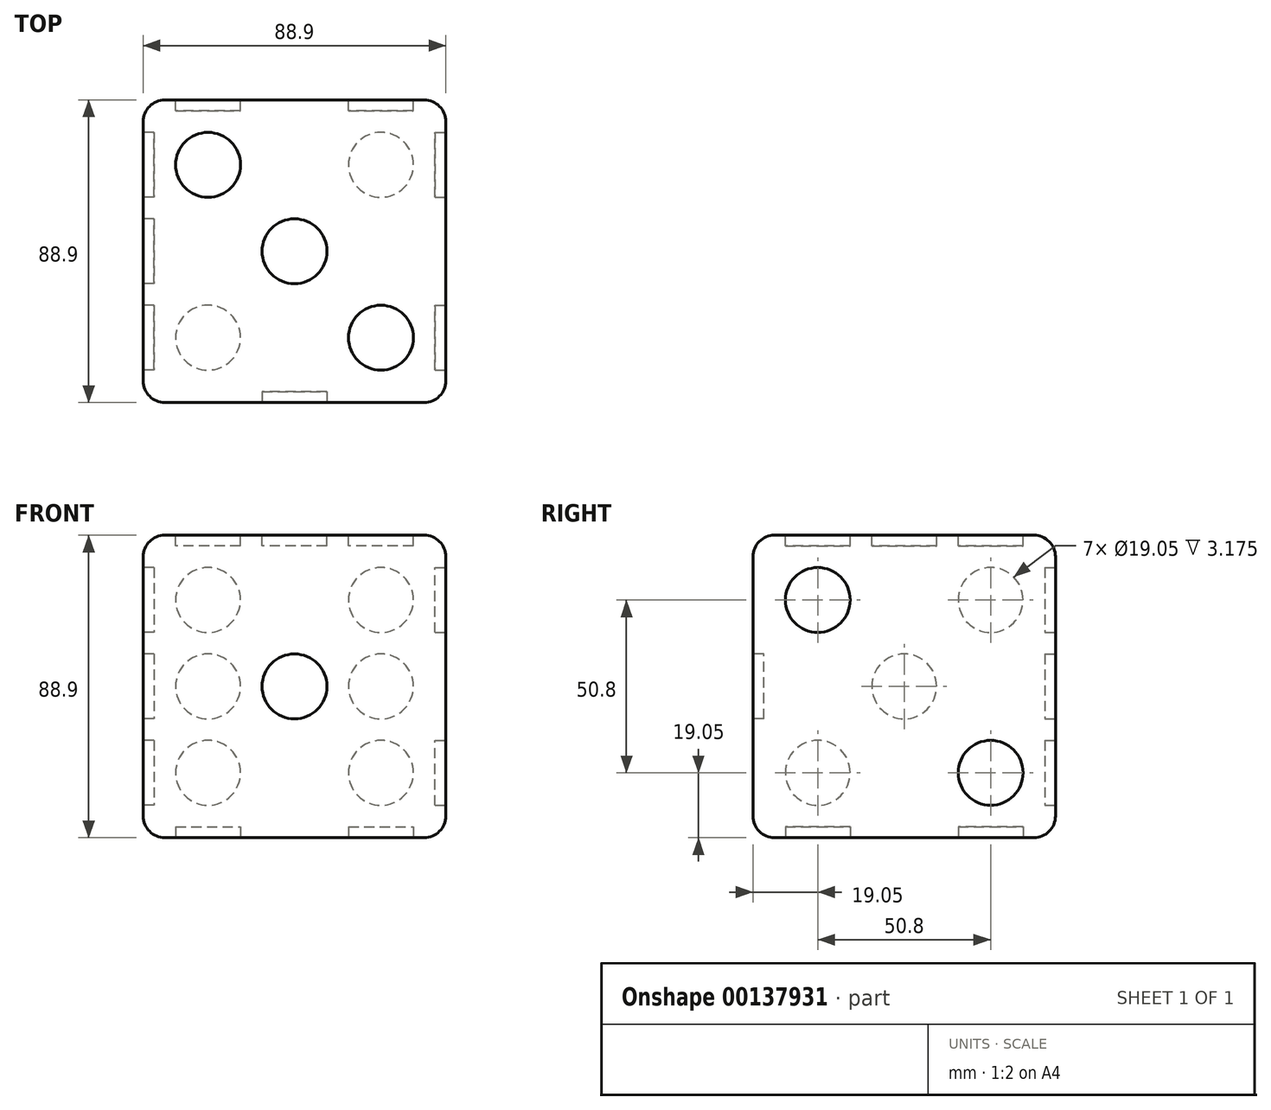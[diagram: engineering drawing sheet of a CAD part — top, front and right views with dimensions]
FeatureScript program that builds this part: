
annotation { "Feature Type Name" : "Feature", "Feature Type Description" : "" }
export const myFeature = defineFeature(function(context is Context, id is Id, definition is map)
    precondition{}
    {
        {
            var Q0;
            Q0=qCreatedBy(makeId("Top.planeOp"),FACE);
            var sketch = newSketch(context, id + "F0", { "sketchPlane" : qUnion([Q0])});
            skLineSegment(sketch, "E0.bottom", {"start": v(44.45, -44.45) * mm, "end": v(-44.45, -44.45) * mm});
            skLineSegment(sketch, "E0.top", {"start": v(44.45, 44.45) * mm, "end": v(-44.45, 44.45) * mm});
            skLineSegment(sketch, "E0.left", {"start": v(44.45, -44.45) * mm, "end": v(44.45, 44.45) * mm});
            skLineSegment(sketch, "E0.right", {"start": v(-44.45, -44.45) * mm, "end": v(-44.45, 44.45) * mm});
            skPoint(sketch, "E0.middle", {"position": v(0, 0) * mm});
            skSolve(sketch);
        }
        {
            var Q0;
            Q0 = qSketchRegion(id + "F0", true);
            extrude(context, id + "F1", {"entities" : qUnion([Q0]), "depth" : 88.9 * mm, "symmetric" : true});
        }
        {
            var Q0;
            Q0=makeQuery(id+"F1.opExtrude","CAP_FACE",FACE,{"disambiguationData":[OSD([sQuery(id+"F0.wireOp",EDGE,"E0.bottom"),sQuery(id+"F0.wireOp",EDGE,"E0.top"),sQuery(id+"F0.wireOp",EDGE,"E0.left"),sQuery(id+"F0.wireOp",EDGE,"E0.right")])],"isStart":false});
            var Q1;
            Q1=makeQuery(id+"F1.opExtrude","SWEPT_FACE",FACE,{"disambiguationData":[OSD([sQuery(id+"F0.wireOp",EDGE,"E0.bottom")])]});
            var Q2;
            Q2=makeQuery(id+"F1.opExtrude","SWEPT_FACE",FACE,{"disambiguationData":[OSD([sQuery(id+"F0.wireOp",EDGE,"E0.top")])]});
            var Q3;
            Q3=makeQuery(id+"F1.opExtrude","CAP_FACE",FACE,{"disambiguationData":[OSD([sQuery(id+"F0.wireOp",EDGE,"E0.bottom"),sQuery(id+"F0.wireOp",EDGE,"E0.top"),sQuery(id+"F0.wireOp",EDGE,"E0.left"),sQuery(id+"F0.wireOp",EDGE,"E0.right")])],"isStart":true});
            fillet(context, id + "F2", {"entities" : qUnion([Q0, Q1, Q2, Q3]), "radius" : 6.35 * mm, "tangentPropagation" : true, "allowEdgeOverflow" : false});
        }
        {
            var Q0;
            Q0=makeQuery(id+"F1.opExtrude","SWEPT_FACE",FACE,{"disambiguationData":[OSD([sQuery(id+"F0.wireOp",EDGE,"E0.bottom")])]});
            var sketch = newSketch(context, id + "F3", { "sketchPlane" : qUnion([Q0])});
            skLineSegment(sketch, "E1.bottom", {"start": v(34.92, -34.92) * mm, "end": v(-34.92, -34.92) * mm, "construction": true});
            skLineSegment(sketch, "E1.top", {"start": v(34.92, 34.93) * mm, "end": v(-34.92, 34.93) * mm, "construction": true});
            skLineSegment(sketch, "E1.left", {"start": v(34.92, -34.93) * mm, "end": v(34.92, 34.93) * mm, "construction": true});
            skLineSegment(sketch, "E1.right", {"start": v(-34.92, -34.93) * mm, "end": v(-34.92, 34.93) * mm, "construction": true});
            skPoint(sketch, "E1.middle", {"position": v(0, 0) * mm});
            skLineSegment(sketch, "E2", {"start": v(0, 34.93) * mm, "end": v(0, -34.92) * mm, "construction": true});
            skLineSegment(sketch, "E3", {"start": v(34.92, 0) * mm, "end": v(-34.92, 0) * mm, "construction": true});
            skLineSegment(sketch, "E4", {"start": v(-25.4, 34.93) * mm, "end": v(-25.4, -34.92) * mm, "construction": true});
            skLineSegment(sketch, "E5", {"start": v(-34.92, -25.4) * mm, "end": v(34.92, -25.4) * mm, "construction": true});
            skLineSegment(sketch, "E6", {"start": v(25.4, 34.93) * mm, "end": v(25.4, -34.93) * mm, "construction": true});
            skLineSegment(sketch, "E7", {"start": v(-34.92, 25.4) * mm, "end": v(34.92, 25.4) * mm, "construction": true});
            skCircle(sketch, "E8", {"center": v(-25.4, 25.4) * mm, "radius": 9.52 * mm, "construction": true});
            skCircle(sketch, "E9", {"center": v(25.4, 25.4) * mm, "radius": 9.52 * mm, "construction": true});
            skCircle(sketch, "E10", {"center": v(-25.4, -25.4) * mm, "radius": 9.52 * mm, "construction": true});
            skCircle(sketch, "E11", {"center": v(25.4, -25.4) * mm, "radius": 9.52 * mm, "construction": true});
            skCircle(sketch, "E12", {"center": v(-25.4, 0) * mm, "radius": 9.52 * mm, "construction": true});
            skCircle(sketch, "E13", {"center": v(25.4, 0) * mm, "radius": 9.52 * mm, "construction": true});
            skCircle(sketch, "E14", {"center": v(0, 0) * mm, "radius": 9.52 * mm});
            skCircle(sketch, "E15", {"center": v(0, -25.4) * mm, "radius": 9.52 * mm, "construction": true});
            skCircle(sketch, "E16", {"center": v(0, 25.4) * mm, "radius": 9.52 * mm, "construction": true});
            skSolve(sketch);
        }
        {
            var Q0;
            Q0=makeQuery(id+"F1.opExtrude","CAP_FACE",FACE,{"disambiguationData":[OSD([sQuery(id+"F0.wireOp",EDGE,"E0.bottom"),sQuery(id+"F0.wireOp",EDGE,"E0.top"),sQuery(id+"F0.wireOp",EDGE,"E0.left"),sQuery(id+"F0.wireOp",EDGE,"E0.right")])],"isStart":true});
            var sketch = newSketch(context, id + "F4", { "sketchPlane" : qUnion([Q0])});
            skLineSegment(sketch, "E17.bottom", {"start": v(34.93, -34.93) * mm, "end": v(-34.93, -34.93) * mm, "construction": true});
            skLineSegment(sketch, "E17.top", {"start": v(34.92, 34.93) * mm, "end": v(-34.93, 34.93) * mm, "construction": true});
            skLineSegment(sketch, "E17.left", {"start": v(34.92, -34.93) * mm, "end": v(34.92, 34.93) * mm, "construction": true});
            skLineSegment(sketch, "E17.right", {"start": v(-34.93, -34.93) * mm, "end": v(-34.93, 34.93) * mm, "construction": true});
            skPoint(sketch, "E17.middle", {"position": v(0, 0) * mm});
            skLineSegment(sketch, "E18", {"start": v(0, 34.93) * mm, "end": v(0, -34.93) * mm, "construction": true});
            skLineSegment(sketch, "E19", {"start": v(34.93, 0) * mm, "end": v(-34.93, 0) * mm, "construction": true});
            skLineSegment(sketch, "E20", {"start": v(-25.4, 34.93) * mm, "end": v(-25.4, -34.93) * mm, "construction": true});
            skLineSegment(sketch, "E21", {"start": v(-34.92, -25.4) * mm, "end": v(34.92, -25.4) * mm, "construction": true});
            skLineSegment(sketch, "E22", {"start": v(25.4, 34.93) * mm, "end": v(25.4, -34.93) * mm, "construction": true});
            skLineSegment(sketch, "E23", {"start": v(-34.92, 25.4) * mm, "end": v(34.92, 25.4) * mm, "construction": true});
            skCircle(sketch, "E24", {"center": v(-25.4, 25.4) * mm, "radius": 9.52 * mm});
            skCircle(sketch, "E25", {"center": v(25.4, 25.4) * mm, "radius": 9.52 * mm});
            skCircle(sketch, "E26", {"center": v(-25.4, -25.4) * mm, "radius": 9.52 * mm});
            skCircle(sketch, "E27", {"center": v(25.4, -25.4) * mm, "radius": 9.52 * mm});
            skCircle(sketch, "E28", {"center": v(-25.4, 0) * mm, "radius": 9.52 * mm, "construction": true});
            skCircle(sketch, "E29", {"center": v(25.4, 0) * mm, "radius": 9.53 * mm, "construction": true});
            skCircle(sketch, "E30", {"center": v(0, 0) * mm, "radius": 9.52 * mm, "construction": true});
            skCircle(sketch, "E31", {"center": v(0, -25.4) * mm, "radius": 9.52 * mm, "construction": true});
            skCircle(sketch, "E32", {"center": v(0, 25.4) * mm, "radius": 9.52 * mm, "construction": true});
            skSolve(sketch);
        }
        {
            var Q0;
            Q0=makeQuery(id+"F1.opExtrude","SWEPT_FACE",FACE,{"disambiguationData":[OSD([sQuery(id+"F0.wireOp",EDGE,"E0.left")])]});
            var sketch = newSketch(context, id + "F5", { "sketchPlane" : qUnion([Q0])});
            skLineSegment(sketch, "E33.bottom", {"start": v(34.92, -34.93) * mm, "end": v(-34.92, -34.93) * mm, "construction": true});
            skLineSegment(sketch, "E33.top", {"start": v(34.92, 34.93) * mm, "end": v(-34.93, 34.93) * mm, "construction": true});
            skLineSegment(sketch, "E33.left", {"start": v(34.92, -34.93) * mm, "end": v(34.92, 34.93) * mm, "construction": true});
            skLineSegment(sketch, "E33.right", {"start": v(-34.92, -34.93) * mm, "end": v(-34.92, 34.92) * mm, "construction": true});
            skPoint(sketch, "E33.middle", {"position": v(0, 0) * mm});
            skLineSegment(sketch, "E34", {"start": v(0, 34.93) * mm, "end": v(0, -34.93) * mm, "construction": true});
            skLineSegment(sketch, "E35", {"start": v(34.92, 0) * mm, "end": v(-34.92, 0) * mm, "construction": true});
            skLineSegment(sketch, "E36", {"start": v(-25.4, 34.93) * mm, "end": v(-25.4, -34.93) * mm, "construction": true});
            skLineSegment(sketch, "E37", {"start": v(-34.92, -25.4) * mm, "end": v(34.92, -25.4) * mm, "construction": true});
            skLineSegment(sketch, "E38", {"start": v(25.4, 34.93) * mm, "end": v(25.4, -34.93) * mm, "construction": true});
            skLineSegment(sketch, "E39", {"start": v(-34.92, 25.4) * mm, "end": v(34.92, 25.4) * mm, "construction": true});
            skCircle(sketch, "E40", {"center": v(-25.4, 25.4) * mm, "radius": 9.53 * mm});
            skCircle(sketch, "E41", {"center": v(25.4, 25.4) * mm, "radius": 9.53 * mm, "construction": true});
            skCircle(sketch, "E42", {"center": v(-25.4, -25.4) * mm, "radius": 9.53 * mm, "construction": true});
            skCircle(sketch, "E43", {"center": v(25.4, -25.4) * mm, "radius": 9.53 * mm});
            skCircle(sketch, "E44", {"center": v(-25.4, 0) * mm, "radius": 9.53 * mm, "construction": true});
            skCircle(sketch, "E45", {"center": v(25.4, 0) * mm, "radius": 9.52 * mm, "construction": true});
            skCircle(sketch, "E46", {"center": v(0, 0) * mm, "radius": 9.53 * mm, "construction": true});
            skCircle(sketch, "E47", {"center": v(0, -25.4) * mm, "radius": 9.53 * mm, "construction": true});
            skCircle(sketch, "E48", {"center": v(0, 25.4) * mm, "radius": 9.53 * mm, "construction": true});
            skLineSegment(sketch, "E49.0.0", {"start": v(44.45, 38.1) * mm, "end": v(44.45, -38.1) * mm, "construction": true});
            skLineSegment(sketch, "E49.0.2", {"start": v(44.45, -38.1) * mm, "end": v(44.45, 38.1) * mm, "construction": true});
            skLineSegment(sketch, "E50.0.1", {"start": v(-38.1, -44.45) * mm, "end": v(38.1, -44.45) * mm, "construction": true});
            skLineSegment(sketch, "E50.0.3", {"start": v(38.1, -44.45) * mm, "end": v(-38.1, -44.45) * mm, "construction": true});
            skSolve(sketch);
        }
        {
            var Q0;
            Q0=makeQuery(id+"F1.opExtrude","CAP_FACE",FACE,{"disambiguationData":[OSD([sQuery(id+"F0.wireOp",EDGE,"E0.bottom"),sQuery(id+"F0.wireOp",EDGE,"E0.top"),sQuery(id+"F0.wireOp",EDGE,"E0.left"),sQuery(id+"F0.wireOp",EDGE,"E0.right")])],"isStart":false});
            var sketch = newSketch(context, id + "F6", { "sketchPlane" : qUnion([Q0])});
            skLineSegment(sketch, "E51.bottom", {"start": v(34.93, -34.92) * mm, "end": v(-34.92, -34.92) * mm, "construction": true});
            skLineSegment(sketch, "E51.top", {"start": v(34.92, 34.92) * mm, "end": v(-34.92, 34.92) * mm, "construction": true});
            skLineSegment(sketch, "E51.left", {"start": v(34.92, -34.93) * mm, "end": v(34.92, 34.92) * mm, "construction": true});
            skLineSegment(sketch, "E51.right", {"start": v(-34.92, -34.93) * mm, "end": v(-34.92, 34.93) * mm, "construction": true});
            skPoint(sketch, "E51.middle", {"position": v(0, 0) * mm});
            skLineSegment(sketch, "E52", {"start": v(0, 34.92) * mm, "end": v(0, -34.93) * mm, "construction": true});
            skLineSegment(sketch, "E53", {"start": v(34.93, 0) * mm, "end": v(-34.92, 0) * mm, "construction": true});
            skLineSegment(sketch, "E54", {"start": v(-25.4, 34.92) * mm, "end": v(-25.4, -34.92) * mm, "construction": true});
            skLineSegment(sketch, "E55", {"start": v(-34.92, -25.4) * mm, "end": v(34.93, -25.4) * mm, "construction": true});
            skLineSegment(sketch, "E56", {"start": v(25.4, 34.92) * mm, "end": v(25.4, -34.92) * mm, "construction": true});
            skLineSegment(sketch, "E57", {"start": v(-34.92, 25.4) * mm, "end": v(34.93, 25.4) * mm, "construction": true});
            skCircle(sketch, "E58", {"center": v(-25.4, 25.4) * mm, "radius": 9.53 * mm});
            skCircle(sketch, "E59", {"center": v(25.4, 25.4) * mm, "radius": 9.53 * mm, "construction": true});
            skCircle(sketch, "E60", {"center": v(-25.4, -25.4) * mm, "radius": 9.53 * mm, "construction": true});
            skCircle(sketch, "E61", {"center": v(25.4, -25.4) * mm, "radius": 9.53 * mm});
            skCircle(sketch, "E62", {"center": v(-25.4, 0) * mm, "radius": 9.52 * mm, "construction": true});
            skCircle(sketch, "E63", {"center": v(25.4, 0) * mm, "radius": 9.52 * mm, "construction": true});
            skCircle(sketch, "E64", {"center": v(0, 0) * mm, "radius": 9.53 * mm});
            skCircle(sketch, "E65", {"center": v(0, -25.4) * mm, "radius": 9.53 * mm, "construction": true});
            skCircle(sketch, "E66", {"center": v(0, 25.4) * mm, "radius": 9.53 * mm, "construction": true});
            skSolve(sketch);
        }
        {
            var Q0;
            Q0=makeQuery(id+"F1.opExtrude","SWEPT_FACE",FACE,{"disambiguationData":[OSD([sQuery(id+"F0.wireOp",EDGE,"E0.top")])]});
            var sketch = newSketch(context, id + "F7", { "sketchPlane" : qUnion([Q0])});
            skLineSegment(sketch, "E67.bottom", {"start": v(34.92, -34.92) * mm, "end": v(-34.92, -34.92) * mm, "construction": true});
            skLineSegment(sketch, "E67.top", {"start": v(34.92, 34.93) * mm, "end": v(-34.92, 34.93) * mm, "construction": true});
            skLineSegment(sketch, "E67.left", {"start": v(34.92, -34.92) * mm, "end": v(34.92, 34.93) * mm, "construction": true});
            skLineSegment(sketch, "E67.right", {"start": v(-34.92, -34.93) * mm, "end": v(-34.92, 34.93) * mm, "construction": true});
            skPoint(sketch, "E67.middle", {"position": v(0, 0) * mm});
            skLineSegment(sketch, "E68", {"start": v(0, 34.93) * mm, "end": v(0, -34.92) * mm, "construction": true});
            skLineSegment(sketch, "E69", {"start": v(34.92, 0) * mm, "end": v(-34.92, 0) * mm, "construction": true});
            skLineSegment(sketch, "E70", {"start": v(-25.4, 34.93) * mm, "end": v(-25.4, -34.93) * mm, "construction": true});
            skLineSegment(sketch, "E71", {"start": v(-34.92, -25.4) * mm, "end": v(34.92, -25.4) * mm, "construction": true});
            skLineSegment(sketch, "E72", {"start": v(25.4, 34.93) * mm, "end": v(25.4, -34.93) * mm, "construction": true});
            skLineSegment(sketch, "E73", {"start": v(-34.92, 25.4) * mm, "end": v(34.92, 25.4) * mm, "construction": true});
            skCircle(sketch, "E74", {"center": v(-25.4, 25.4) * mm, "radius": 9.52 * mm});
            skCircle(sketch, "E75", {"center": v(25.4, 25.4) * mm, "radius": 9.52 * mm});
            skCircle(sketch, "E76", {"center": v(-25.4, -25.4) * mm, "radius": 9.52 * mm});
            skCircle(sketch, "E77", {"center": v(25.4, -25.4) * mm, "radius": 9.52 * mm});
            skCircle(sketch, "E78", {"center": v(-25.4, 0) * mm, "radius": 9.52 * mm});
            skCircle(sketch, "E79", {"center": v(25.4, 0) * mm, "radius": 9.52 * mm});
            skCircle(sketch, "E80", {"center": v(0, 0) * mm, "radius": 9.52 * mm, "construction": true});
            skCircle(sketch, "E81", {"center": v(0, -25.4) * mm, "radius": 9.52 * mm, "construction": true});
            skCircle(sketch, "E82", {"center": v(0, 25.4) * mm, "radius": 9.52 * mm, "construction": true});
            skSolve(sketch);
        }
        {
            var Q0;
            Q0=makeQuery(id+"F1.opExtrude","SWEPT_FACE",FACE,{"disambiguationData":[OSD([sQuery(id+"F0.wireOp",EDGE,"E0.right")])]});
            var sketch = newSketch(context, id + "F8", { "sketchPlane" : qUnion([Q0])});
            skLineSegment(sketch, "E83.bottom", {"start": v(34.93, -34.93) * mm, "end": v(-34.92, -34.93) * mm, "construction": true});
            skLineSegment(sketch, "E83.top", {"start": v(34.92, 34.93) * mm, "end": v(-34.92, 34.93) * mm, "construction": true});
            skLineSegment(sketch, "E83.left", {"start": v(34.92, -34.92) * mm, "end": v(34.92, 34.93) * mm, "construction": true});
            skLineSegment(sketch, "E83.right", {"start": v(-34.92, -34.92) * mm, "end": v(-34.92, 34.93) * mm, "construction": true});
            skPoint(sketch, "E83.middle", {"position": v(0, 0) * mm});
            skLineSegment(sketch, "E84", {"start": v(0, 34.93) * mm, "end": v(0, -34.92) * mm, "construction": true});
            skLineSegment(sketch, "E85", {"start": v(34.92, 0) * mm, "end": v(-34.92, 0) * mm, "construction": true});
            skLineSegment(sketch, "E86", {"start": v(-25.4, 34.93) * mm, "end": v(-25.4, -34.93) * mm, "construction": true});
            skLineSegment(sketch, "E87", {"start": v(-34.92, -25.4) * mm, "end": v(34.92, -25.4) * mm, "construction": true});
            skLineSegment(sketch, "E88", {"start": v(25.4, 34.93) * mm, "end": v(25.4, -34.93) * mm, "construction": true});
            skLineSegment(sketch, "E89", {"start": v(-34.92, 25.4) * mm, "end": v(34.92, 25.4) * mm, "construction": true});
            skCircle(sketch, "E90", {"center": v(-25.4, 25.4) * mm, "radius": 9.53 * mm});
            skCircle(sketch, "E91", {"center": v(25.4, 25.4) * mm, "radius": 9.53 * mm});
            skCircle(sketch, "E92", {"center": v(-25.4, -25.4) * mm, "radius": 9.53 * mm});
            skCircle(sketch, "E93", {"center": v(25.4, -25.4) * mm, "radius": 9.53 * mm});
            skCircle(sketch, "E94", {"center": v(-25.4, 0) * mm, "radius": 9.52 * mm, "construction": true});
            skCircle(sketch, "E95", {"center": v(25.4, 0) * mm, "radius": 9.52 * mm, "construction": true});
            skCircle(sketch, "E96", {"center": v(0, 0) * mm, "radius": 9.53 * mm});
            skCircle(sketch, "E97", {"center": v(0, -25.4) * mm, "radius": 9.53 * mm, "construction": true});
            skCircle(sketch, "E98", {"center": v(0, 25.4) * mm, "radius": 9.53 * mm, "construction": true});
            skSolve(sketch);
        }
        {
            var Q0;
            Q0 = qSketchRegion(id + "F3", true);
            extrude(context, id + "F9", {"entities" : qUnion([Q0]), "operationType" : NewBodyOperationType.REMOVE, "oppositeDirection" : true, "depth" : 3.17 * mm});
        }
        {
            var Q0;
            Q0 = qSketchRegion(id + "F4", true);
            extrude(context, id + "F10", {"entities" : qUnion([Q0]), "operationType" : NewBodyOperationType.REMOVE, "oppositeDirection" : true, "depth" : 3.17 * mm});
        }
        {
            var Q0;
            Q0 = qSketchRegion(id + "F5", true);
            extrude(context, id + "F11", {"entities" : qUnion([Q0]), "operationType" : NewBodyOperationType.REMOVE, "oppositeDirection" : true, "depth" : 3.17 * mm});
        }
        {
            var Q0;
            Q0 = qSketchRegion(id + "F6", true);
            extrude(context, id + "F12", {"entities" : qUnion([Q0]), "operationType" : NewBodyOperationType.REMOVE, "oppositeDirection" : true, "depth" : 3.17 * mm});
        }
        {
            var Q0;
            Q0 = qSketchRegion(id + "F7", true);
            extrude(context, id + "F13", {"entities" : qUnion([Q0]), "operationType" : NewBodyOperationType.REMOVE, "oppositeDirection" : true, "depth" : 3.17 * mm});
        }
        {
            var Q0;
            Q0 = qSketchRegion(id + "F8", true);
            extrude(context, id + "F14", {"entities" : qUnion([Q0]), "operationType" : NewBodyOperationType.REMOVE, "oppositeDirection" : true, "depth" : 3.17 * mm});
        }
    });
